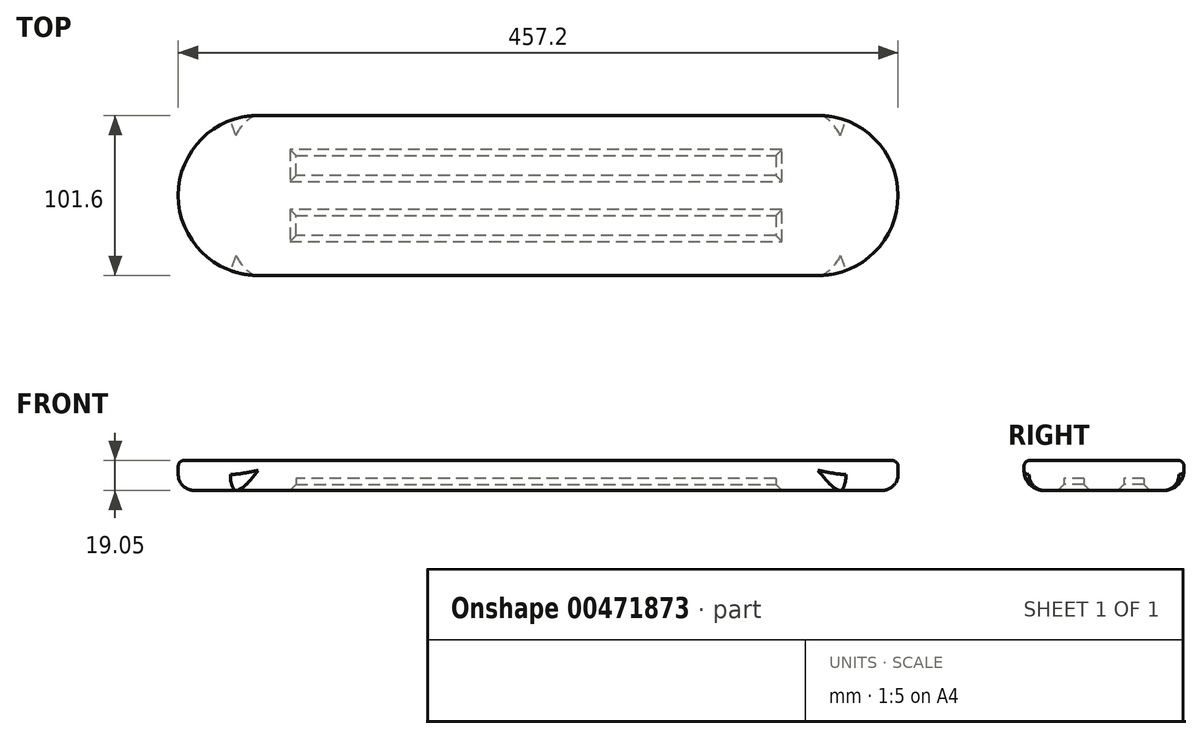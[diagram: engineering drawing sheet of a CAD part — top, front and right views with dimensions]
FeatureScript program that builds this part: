
annotation { "Feature Type Name" : "Feature", "Feature Type Description" : "" }
export const myFeature = defineFeature(function(context is Context, id is Id, definition is map)
    precondition{}
    {
        {
            var Q0;
            Q0=qCreatedBy(makeId("Top.planeOp"),FACE);
            var sketch = newSketch(context, id + "F0", { "sketchPlane" : qUnion([Q0])});
            skLineSegment(sketch, "E0.bottom", {"start": v(-163.92, -92.64) * mm, "end": v(191.68, -92.64) * mm});
            skLineSegment(sketch, "E0.top", {"start": v(-163.92, 8.96) * mm, "end": v(191.68, 8.96) * mm});
            skLineSegment(sketch, "E0.left", {"start": v(-214.72, -41.84) * mm, "end": v(-214.72, -41.84) * mm});
            skLineSegment(sketch, "E0.right", {"start": v(242.48, -41.84) * mm, "end": v(242.48, -41.84) * mm});
            skPoint(sketch, "E1.visualSharp", {"position": v(-214.72, 8.96) * mm});
            skArc(sketch, "E1.filletArc", {"start": v(-163.92, 8.96) * mm, "mid": v(-199.85, -5.92) * mm, "end": v(-214.72, -41.84) * mm});
            skPoint(sketch, "E2.visualSharp", {"position": v(-214.72, -92.64) * mm});
            skArc(sketch, "E2.filletArc", {"start": v(-214.72, -41.84) * mm, "mid": v(-199.85, -77.76) * mm, "end": v(-163.92, -92.64) * mm});
            skPoint(sketch, "E3.visualSharp", {"position": v(242.48, -92.64) * mm});
            skArc(sketch, "E3.filletArc", {"start": v(191.68, -92.64) * mm, "mid": v(227.6, -77.76) * mm, "end": v(242.48, -41.84) * mm});
            skPoint(sketch, "E4.visualSharp", {"position": v(242.48, 8.96) * mm});
            skArc(sketch, "E4.filletArc", {"start": v(242.48, -41.84) * mm, "mid": v(227.6, -5.92) * mm, "end": v(191.68, 8.96) * mm});
            skSolve(sketch);
        }
        {
            var Q0;
            Q0=makeQuery(id+"F0.imprint","IMPRINT",FACE,{"disambiguationData":[TD([[makeQuery(id+"F0.imprint","IMPRINT",EDGE,{"derivedFrom":sQuery(id+"F0.wireOp",EDGE,"E0.bottom")}),1.0]])]});
            extrude(context, id + "F1", {"entities" : qUnion([Q0]), "depth" : 19.05 * mm});
        }
        {
            var Q0;
            Q0=makeQuery(id+"F1.opExtrude","CAP_FACE",FACE,{"disambiguationData":[OSD([sQuery(id+"F0.wireOp",EDGE,"E0.bottom"),sQuery(id+"F0.wireOp",EDGE,"E0.top"),sQuery(id+"F0.wireOp",EDGE,"E1.filletArc"),sQuery(id+"F0.wireOp",EDGE,"E2.filletArc"),sQuery(id+"F0.wireOp",EDGE,"E3.filletArc"),sQuery(id+"F0.wireOp",EDGE,"E4.filletArc")])],"isStart":false});
            fillet(context, id + "F2", {"entities" : qUnion([Q0]), "radius" : 3.8 * mm, "tangentPropagation" : true, "allowEdgeOverflow" : false});
        }
        {
            var Q0;
            Q0=makeQuery(id+"F1.opExtrude","CAP_EDGE",EDGE,{"disambiguationData":[OSD([sQuery(id+"F0.wireOp",EDGE,"E0.bottom")])],"isStart":true});
            var Q1;
            Q1=makeQuery(id+"F1.opExtrude","CAP_EDGE",EDGE,{"disambiguationData":[OSD([sQuery(id+"F0.wireOp",EDGE,"E0.top")])],"isStart":true});
            fillet(context, id + "F3", {"entities" : qUnion([Q0, Q1]), "radius" : 12.7 * mm, "allowEdgeOverflow" : false});
        }
        {
            var Q0;
            Q0=makeQuery(id+"F1.opExtrude","CAP_EDGE",EDGE,{"disambiguationData":[OSD([sQuery(id+"F0.wireOp",EDGE,"E3.filletArc"),sQuery(id+"F0.wireOp",EDGE,"E4.filletArc")])],"isStart":true});
            var Q1;
            Q1=makeQuery(id+"F1.opExtrude","CAP_EDGE",EDGE,{"disambiguationData":[OSD([sQuery(id+"F0.wireOp",EDGE,"E1.filletArc"),sQuery(id+"F0.wireOp",EDGE,"E2.filletArc")])],"isStart":true});
            fillet(context, id + "F4", {"entities" : qUnion([Q0, Q1]), "radius" : 10.16 * mm, "tangentPropagation" : true, "allowEdgeOverflow" : false});
        }
        {
            var Q0;
            Q0=makeQuery(id+"F1.opExtrude","CAP_FACE",FACE,{"disambiguationData":[OSD([sQuery(id+"F0.wireOp",EDGE,"E0.bottom"),sQuery(id+"F0.wireOp",EDGE,"E0.top"),sQuery(id+"F0.wireOp",EDGE,"E1.filletArc"),sQuery(id+"F0.wireOp",EDGE,"E2.filletArc"),sQuery(id+"F0.wireOp",EDGE,"E3.filletArc"),sQuery(id+"F0.wireOp",EDGE,"E4.filletArc")])],"isStart":true});
            var sketch = newSketch(context, id + "F5", { "sketchPlane" : qUnion([Q0])});
            skLineSegment(sketch, "E5.bottom", {"start": v(164.83, 16.44) * mm, "end": v(-139.97, 16.44) * mm});
            skLineSegment(sketch, "E5.top", {"start": v(164.83, 29.14) * mm, "end": v(-139.97, 29.14) * mm});
            skLineSegment(sketch, "E5.left", {"start": v(164.83, 16.44) * mm, "end": v(164.83, 29.14) * mm});
            skLineSegment(sketch, "E5.right", {"start": v(-139.97, 16.44) * mm, "end": v(-139.97, 29.14) * mm});
            skLineSegment(sketch, "E6.0.1.0", {"start": v(164.83, 54.54) * mm, "end": v(-139.97, 54.54) * mm});
            skLineSegment(sketch, "E6.0.1.1", {"start": v(164.83, 67.24) * mm, "end": v(-139.97, 67.24) * mm});
            skLineSegment(sketch, "E6.0.1.2", {"start": v(164.83, 54.54) * mm, "end": v(164.83, 67.24) * mm});
            skLineSegment(sketch, "E6.0.1.3", {"start": v(-139.97, 54.54) * mm, "end": v(-139.97, 67.24) * mm});
            skLineSegment(sketch, "E6.direction1", {"start": v(-139.97, 16.44) * mm, "end": v(-165.37, 16.44) * mm, "construction": true});
            skLineSegment(sketch, "E6.direction2", {"start": v(-139.97, 16.44) * mm, "end": v(-139.97, 54.54) * mm, "construction": true});
            skSolve(sketch);
        }
        {
            var Q0;
            Q0 = qSketchRegion(id + "F5", true);
            extrude(context, id + "F6", {"entities" : qUnion([Q0]), "operationType" : NewBodyOperationType.REMOVE, "oppositeDirection" : true, "depth" : 7.62 * mm});
        }
        {
            var Q0;
            Q0=makeQuery(id+"F1.opExtrude","CAP_FACE",FACE,{"disambiguationData":[OSD([sQuery(id+"F0.wireOp",EDGE,"E0.bottom"),sQuery(id+"F0.wireOp",EDGE,"E0.top"),sQuery(id+"F0.wireOp",EDGE,"E1.filletArc"),sQuery(id+"F0.wireOp",EDGE,"E2.filletArc"),sQuery(id+"F0.wireOp",EDGE,"E3.filletArc"),sQuery(id+"F0.wireOp",EDGE,"E4.filletArc")])],"isStart":true});
            chamfer(context, id + "F7", {"entities" : qUnion([Q0]), "width" : 3.8 * mm});
        }
    });
